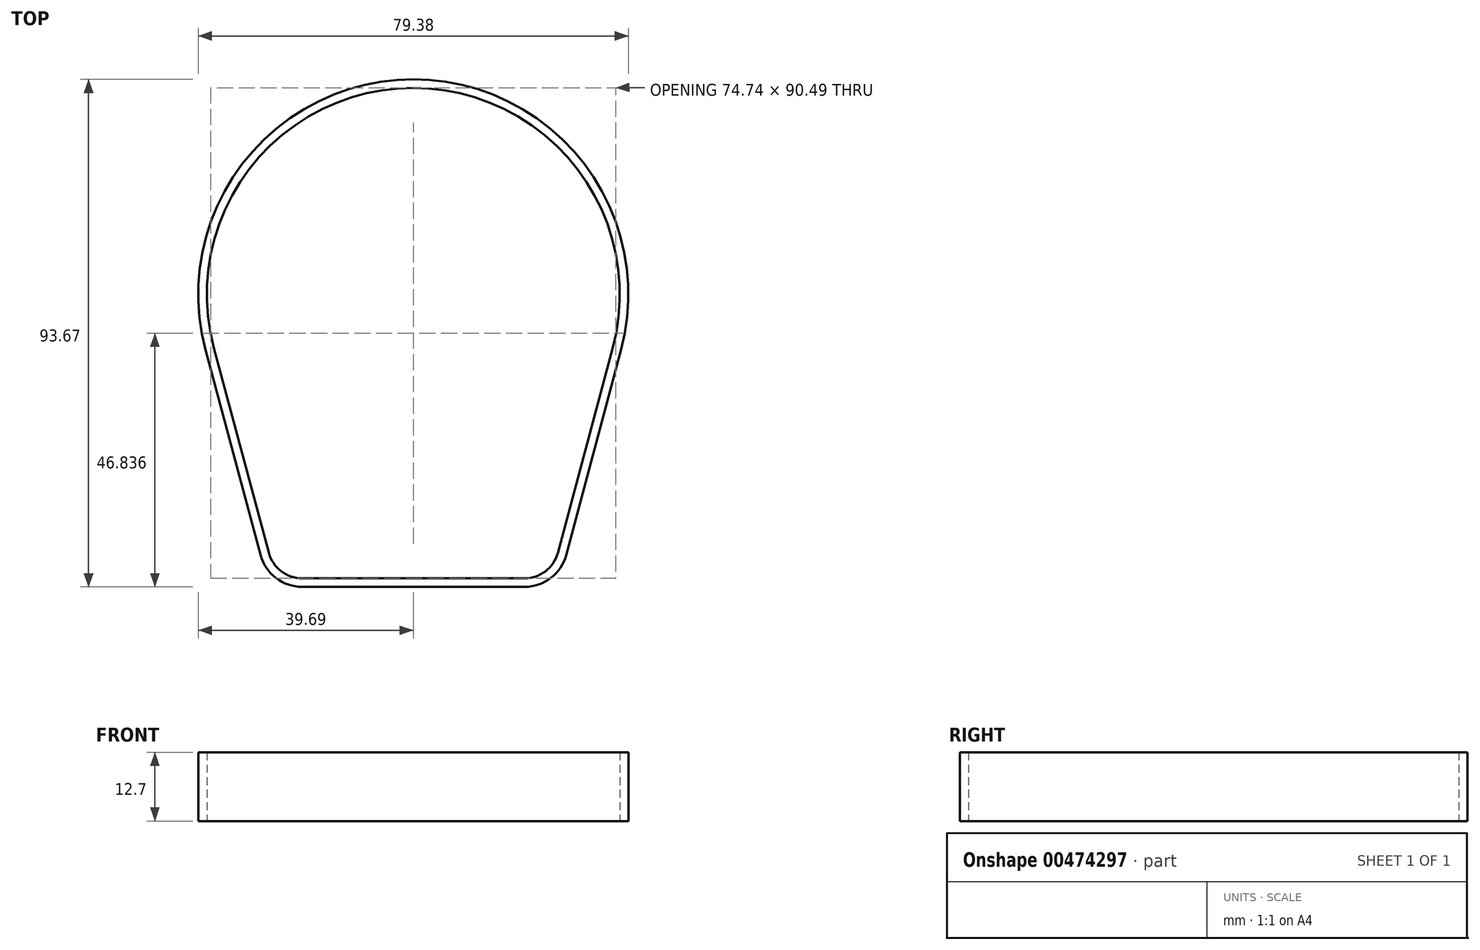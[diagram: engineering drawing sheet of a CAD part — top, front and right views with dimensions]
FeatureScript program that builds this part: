
annotation { "Feature Type Name" : "Feature", "Feature Type Description" : "" }
export const myFeature = defineFeature(function(context is Context, id is Id, definition is map)
    precondition{}
    {
        {
            var Q0;
            Q0=qCreatedBy(makeId("Top.planeOp"),FACE);
            var sketch = newSketch(context, id + "F0", { "sketchPlane" : qUnion([Q0])});
            skArc(sketch, "E0", {"start": v(36.8, -9.87) * mm, "mid": v(0, 38.1) * mm, "end": v(-36.8, -9.87) * mm});
            skLineSegment(sketch, "E1", {"start": v(-36.8, -9.87) * mm, "end": v(-26.66, -47.68) * mm});
            skLineSegment(sketch, "E2", {"start": v(-20.53, -52.39) * mm, "end": v(20.53, -52.39) * mm});
            skLineSegment(sketch, "E3", {"start": v(26.66, -47.68) * mm, "end": v(36.8, -9.87) * mm});
            skPoint(sketch, "E4.visualSharp", {"position": v(-25.4, -52.39) * mm});
            skArc(sketch, "E4.filletArc", {"start": v(-26.66, -47.68) * mm, "mid": v(-24.4, -51.08) * mm, "end": v(-20.53, -52.39) * mm});
            skPoint(sketch, "E5.visualSharp", {"position": v(25.4, -52.39) * mm});
            skArc(sketch, "E5.filletArc", {"start": v(20.53, -52.39) * mm, "mid": v(24.4, -51.08) * mm, "end": v(26.66, -47.68) * mm});
            skArc(sketch, "E6.0", {"start": v(20.53, -53.98) * mm, "mid": v(25.36, -52.34) * mm, "end": v(28.2, -48.1) * mm});
            skArc(sketch, "E6.1", {"start": v(38.33, -10.28) * mm, "mid": v(0, 39.69) * mm, "end": v(-38.33, -10.28) * mm});
            skLineSegment(sketch, "E6.2", {"start": v(-38.33, -10.28) * mm, "end": v(-28.2, -48.1) * mm});
            skLineSegment(sketch, "E6.3", {"start": v(28.2, -48.1) * mm, "end": v(38.33, -10.28) * mm});
            skArc(sketch, "E6.4", {"start": v(-28.2, -48.1) * mm, "mid": v(-25.36, -52.34) * mm, "end": v(-20.53, -53.98) * mm});
            skLineSegment(sketch, "E6.5", {"start": v(-20.53, -53.98) * mm, "end": v(20.53, -53.98) * mm});
            skSolve(sketch);
        }
        {
            var Q0;
            Q0 = qSketchRegion(id + "F0", true);
            extrude(context, id + "F1", {"entities" : qUnion([Q0]), "depth" : 12.7 * mm});
        }
    });
